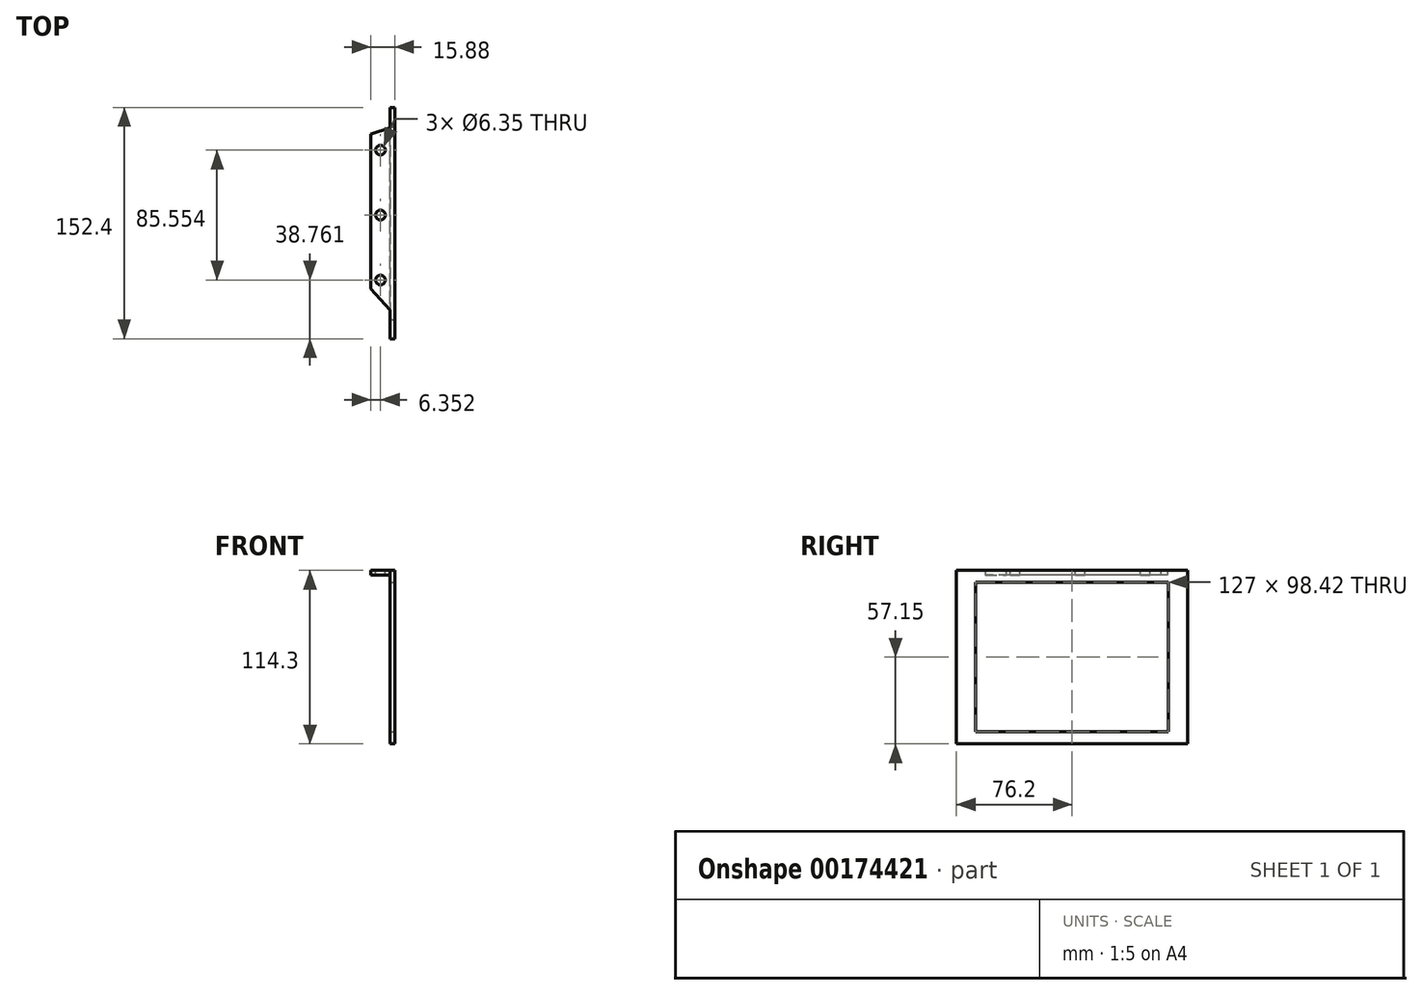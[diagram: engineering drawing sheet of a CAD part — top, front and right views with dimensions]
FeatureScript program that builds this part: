
annotation { "Feature Type Name" : "Feature", "Feature Type Description" : "" }
export const myFeature = defineFeature(function(context is Context, id is Id, definition is map)
    precondition{}
    {
        {
            var Q0;
            Q0=qCreatedBy(makeId("Top.planeOp"),FACE);
            var sketch = newSketch(context, id + "F0", { "sketchPlane" : qUnion([Q0])});
            skLineSegment(sketch, "E0.bottom", {"start": v(1.59, -76.2) * mm, "end": v(-1.59, -76.2) * mm});
            skLineSegment(sketch, "E0.top", {"start": v(1.59, 76.2) * mm, "end": v(-1.59, 76.2) * mm});
            skLineSegment(sketch, "E0.left", {"start": v(1.59, -76.2) * mm, "end": v(1.59, 76.2) * mm});
            skLineSegment(sketch, "E0.right", {"start": v(-1.59, -76.2) * mm, "end": v(-1.59, 76.2) * mm});
            skPoint(sketch, "E0.middle", {"position": v(0, 0) * mm});
            skSolve(sketch);
        }
        {
            var Q0;
            Q0 = qSketchRegion(id + "F0", true);
            extrude(context, id + "F1", {"entities" : qUnion([Q0]), "depth" : 114.3 * mm});
        }
        {
            var Q0;
            Q0=makeQuery(id+"F1.opExtrude","SWEPT_FACE",FACE,{"disambiguationData":[OSD([sQuery(id+"F0.wireOp",EDGE,"E0.left")])]});
            var sketch = newSketch(context, id + "F2", { "sketchPlane" : qUnion([Q0])});
            skLineSegment(sketch, "E1.bottom", {"start": v(63.5, 106.36) * mm, "end": v(-63.5, 106.36) * mm});
            skLineSegment(sketch, "E1.top", {"start": v(63.5, 7.94) * mm, "end": v(-63.5, 7.94) * mm});
            skLineSegment(sketch, "E1.left", {"start": v(63.5, 106.36) * mm, "end": v(63.5, 7.94) * mm});
            skLineSegment(sketch, "E1.right", {"start": v(-63.5, 106.36) * mm, "end": v(-63.5, 7.94) * mm});
            skPoint(sketch, "E1.middle", {"position": v(0, 57.15) * mm});
            skPoint(sketch, "E1.middle.positionSnap0", {"position": v(-76.2, 57.15) * mm});
            skPoint(sketch, "E1.centerSnap0", {"position": v(-76.2, 57.15) * mm});
            skSolve(sketch);
        }
        {
            var Q0;
            Q0 = qSketchRegion(id + "F2", true);
            extrude(context, id + "F3", {"entities" : qUnion([Q0]), "operationType" : NewBodyOperationType.REMOVE, "oppositeDirection" : true, "depth" : 25.4 * mm});
        }
        {
            var Q0;
            Q0=makeQuery(id+"F1.opExtrude","SWEPT_FACE",FACE,{"disambiguationData":[OSD([sQuery(id+"F0.wireOp",EDGE,"E0.right")])]});
            var sketch = newSketch(context, id + "F4", { "sketchPlane" : qUnion([Q0])});
            skPoint(sketch, "E2", {"position": v(-62.82, 114.3) * mm});
            skPoint(sketch, "E3", {"position": v(57.08, 114.3) * mm});
            skLineSegment(sketch, "E4.bottom", {"start": v(-62.82, 114.3) * mm, "end": v(57.08, 114.3) * mm});
            skLineSegment(sketch, "E4.top", {"start": v(-62.82, 111.13) * mm, "end": v(57.08, 111.13) * mm});
            skLineSegment(sketch, "E4.left", {"start": v(-62.82, 114.3) * mm, "end": v(-62.82, 111.13) * mm});
            skLineSegment(sketch, "E4.right", {"start": v(57.08, 114.3) * mm, "end": v(57.08, 111.13) * mm});
            skSolve(sketch);
        }
        {
            var Q0;
            Q0 = qSketchRegion(id + "F4", true);
            extrude(context, id + "F5", {"entities" : qUnion([Q0]), "operationType" : NewBodyOperationType.ADD, "depth" : 12.7 * mm, "offsetDistance" : 25.4 * mm});
        }
        {
            var Q0;
            Q0=makeQuery(id+"F5.boolean.opBoolean","MERGE",FACE,{"derivedFrom":[makeQuery(id+"F1.opExtrude","CAP_FACE",FACE,{"disambiguationData":[OSD([sQuery(id+"F0.wireOp",EDGE,"E0.bottom"),sQuery(id+"F0.wireOp",EDGE,"E0.top"),sQuery(id+"F0.wireOp",EDGE,"E0.left"),sQuery(id+"F0.wireOp",EDGE,"E0.right")])],"isStart":false}),makeQuery(id+"F5.opExtrude","SWEPT_FACE",FACE,{"disambiguationData":[OSD([sQuery(id+"F4.wireOp",EDGE,"E4.bottom")])]})]});
            var sketch = newSketch(context, id + "F6", { "sketchPlane" : qUnion([Q0])});
            skLineSegment(sketch, "E5", {"start": v(-1.59, 62.82) * mm, "end": v(-14.29, 58.81) * mm});
            skLineSegment(sketch, "E6", {"start": v(-14.29, 58.81) * mm, "end": v(-14.29, 62.82) * mm});
            skLineSegment(sketch, "E7", {"start": v(-14.29, 62.82) * mm, "end": v(-1.59, 62.82) * mm});
            skLineSegment(sketch, "E8", {"start": v(-1.59, -57.08) * mm, "end": v(-14.29, -43.2) * mm});
            skLineSegment(sketch, "E9", {"start": v(-14.29, -43.2) * mm, "end": v(-14.29, -57.08) * mm});
            skLineSegment(sketch, "E10", {"start": v(-14.29, -57.08) * mm, "end": v(-1.59, -57.08) * mm});
            skSolve(sketch);
        }
        {
            var Q0;
            Q0 = qSketchRegion(id + "F6", true);
            extrude(context, id + "F7", {"entities" : qUnion([Q0]), "operationType" : NewBodyOperationType.REMOVE, "oppositeDirection" : true, "depth" : 25.4 * mm, "offsetDistance" : 25.4 * mm});
        }
        {
            var Q0;
            Q0=makeQuery(id+"F5.boolean.opBoolean","MERGE",FACE,{"derivedFrom":[makeQuery(id+"F1.opExtrude","CAP_FACE",FACE,{"disambiguationData":[OSD([sQuery(id+"F0.wireOp",EDGE,"E0.bottom"),sQuery(id+"F0.wireOp",EDGE,"E0.top"),sQuery(id+"F0.wireOp",EDGE,"E0.left"),sQuery(id+"F0.wireOp",EDGE,"E0.right")])],"isStart":false}),makeQuery(id+"F5.opExtrude","SWEPT_FACE",FACE,{"disambiguationData":[OSD([sQuery(id+"F4.wireOp",EDGE,"E4.bottom")])]})]});
            var sketch = newSketch(context, id + "F8", { "sketchPlane" : qUnion([Q0])});
            skLineSegment(sketch, "E11", {"start": v(-7.94, 60.82) * mm, "end": v(-7.94, -50.14) * mm});
            skCircle(sketch, "E12", {"center": v(-7.94, 5.34) * mm, "radius": 3.18 * mm});
            skCircle(sketch, "E13", {"center": v(-7.94, 48.12) * mm, "radius": 3.18 * mm});
            skCircle(sketch, "E14", {"center": v(-7.94, -37.44) * mm, "radius": 3.18 * mm});
            skSolve(sketch);
        }
        {
            var Q0;
            Q0 = qSketchRegion(id + "F8", true);
            extrude(context, id + "F9", {"entities" : qUnion([Q0]), "operationType" : NewBodyOperationType.REMOVE, "oppositeDirection" : true, "depth" : 25.4 * mm, "offsetDistance" : 25.4 * mm});
        }
    });
